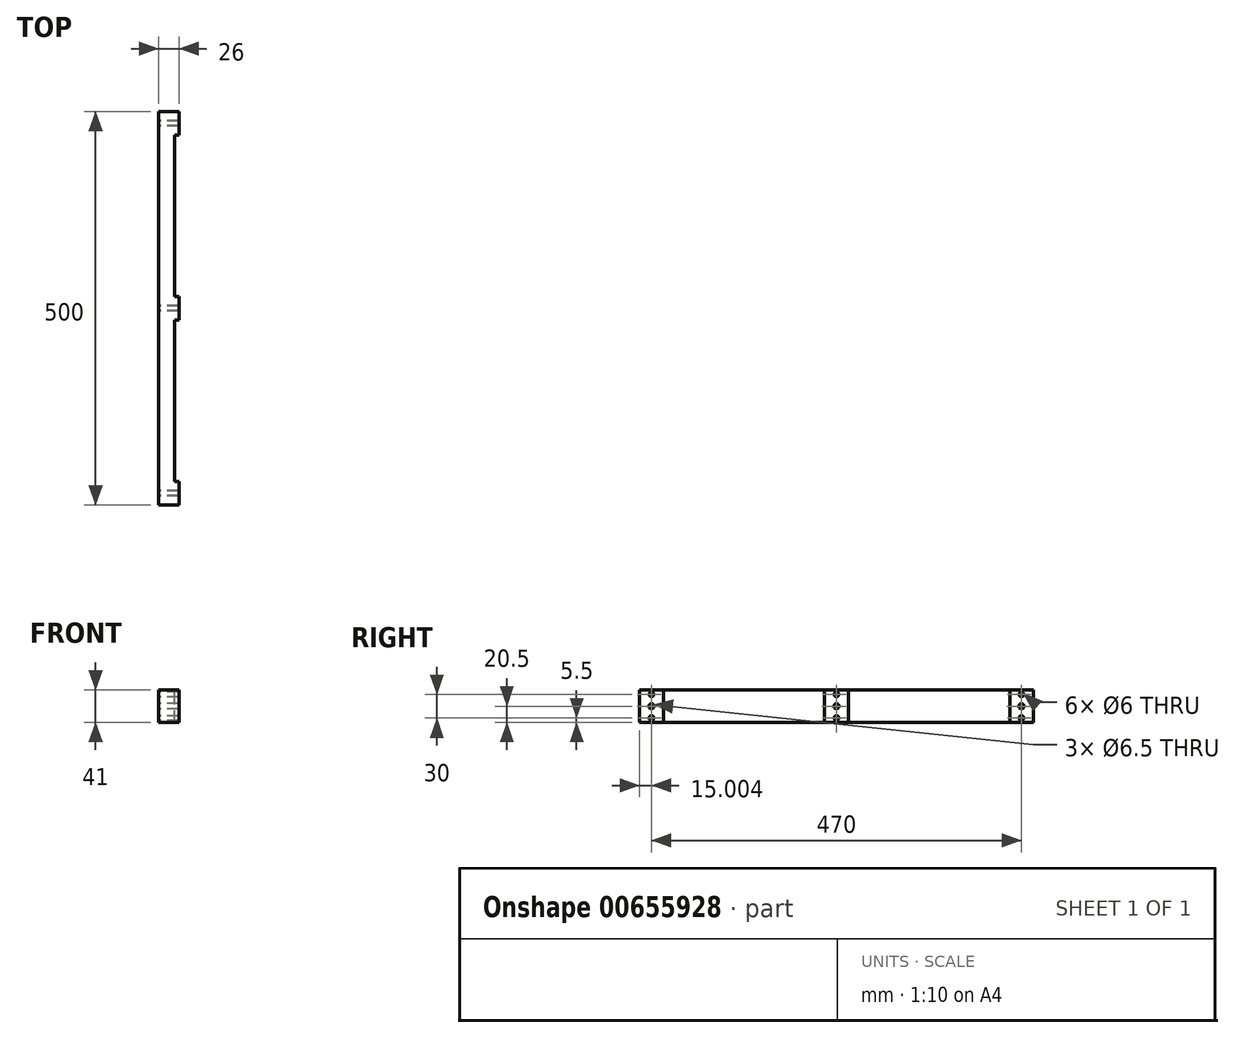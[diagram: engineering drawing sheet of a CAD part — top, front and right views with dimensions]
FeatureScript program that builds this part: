
annotation { "Feature Type Name" : "Feature", "Feature Type Description" : "" }
export const myFeature = defineFeature(function(context is Context, id is Id, definition is map)
    precondition{}
    {
        {
            var Q0;
            Q0=qCreatedBy(makeId("Right.planeOp"),FACE);
            var sketch = newSketch(context, id + "F0", { "sketchPlane" : qUnion([Q0])});
            skLineSegment(sketch, "E0.bottom", {"start": v(-358.97, 48.34) * mm, "end": v(141.03, 48.34) * mm});
            skLineSegment(sketch, "E0.top", {"start": v(-358.97, 7.34) * mm, "end": v(141.03, 7.34) * mm});
            skLineSegment(sketch, "E0.left", {"start": v(-358.97, 48.34) * mm, "end": v(-358.97, 7.34) * mm});
            skLineSegment(sketch, "E0.right", {"start": v(141.03, 48.34) * mm, "end": v(141.03, 7.34) * mm});
            skCircle(sketch, "E1", {"center": v(-343.97, 27.84) * mm, "radius": 3.25 * mm});
            skCircle(sketch, "E2", {"center": v(-108.97, 27.84) * mm, "radius": 3.25 * mm});
            skCircle(sketch, "E3", {"center": v(126.03, 27.84) * mm, "radius": 3.25 * mm});
            skCircle(sketch, "E4", {"center": v(-343.97, 42.84) * mm, "radius": 3 * mm});
            skCircle(sketch, "E5", {"center": v(-343.97, 12.84) * mm, "radius": 3 * mm});
            skCircle(sketch, "E6", {"center": v(-343.97, 27.84) * mm, "radius": 10 * mm, "construction": true});
            skCircle(sketch, "E7", {"center": v(-108.97, 42.84) * mm, "radius": 3 * mm});
            skCircle(sketch, "E8", {"center": v(-108.97, 12.84) * mm, "radius": 3 * mm});
            skCircle(sketch, "E9", {"center": v(126.03, 42.84) * mm, "radius": 3 * mm});
            skCircle(sketch, "E10", {"center": v(126.03, 12.84) * mm, "radius": 3 * mm});
            skCircle(sketch, "E11", {"center": v(-108.97, 27.84) * mm, "radius": 10 * mm, "construction": true});
            skCircle(sketch, "E12", {"center": v(126.03, 27.84) * mm, "radius": 10 * mm, "construction": true});
            skSolve(sketch);
        }
        {
            var Q0;
            Q0=makeQuery(id+"F0.imprint","IMPRINT",FACE,{"disambiguationData":[TD([[makeQuery(id+"F0.imprint","IMPRINT",EDGE,{"derivedFrom":sQuery(id+"F0.wireOp",EDGE,"E0.bottom")}),-1.0]])]});
            extrude(context, id + "F1", {"entities" : qUnion([Q0]), "depth" : 26 * mm, "offsetDistance" : 25 * mm});
        }
        {
            var Q0;
            Q0=makeQuery(id+"F1.opExtrude","SWEPT_FACE",FACE,{"disambiguationData":[OSD([sQuery(id+"F0.wireOp",EDGE,"E0.bottom")])]});
            var sketch = newSketch(context, id + "F2", { "sketchPlane" : qUnion([Q0])});
            skLineSegment(sketch, "E13.bottom", {"start": v(26, -328.97) * mm, "end": v(20, -328.97) * mm});
            skLineSegment(sketch, "E13.top", {"start": v(26, -123.97) * mm, "end": v(20, -123.97) * mm});
            skLineSegment(sketch, "E13.left", {"start": v(26, -328.97) * mm, "end": v(26, -123.97) * mm});
            skLineSegment(sketch, "E13.right", {"start": v(20, -328.97) * mm, "end": v(20, -123.97) * mm});
            skLineSegment(sketch, "E14.bottom", {"start": v(26, 111.03) * mm, "end": v(20, 111.03) * mm});
            skLineSegment(sketch, "E14.top", {"start": v(26, -93.97) * mm, "end": v(20, -93.97) * mm});
            skLineSegment(sketch, "E14.left", {"start": v(26, 111.03) * mm, "end": v(26, -93.97) * mm});
            skLineSegment(sketch, "E14.right", {"start": v(20, 111.03) * mm, "end": v(20, -93.97) * mm});
            skSolve(sketch);
        }
        {
            var Q0;
            Q0 = qSketchRegion(id + "F2", true);
            var Q1;
            Q1=makeQuery(id+"F1.opExtrude","SWEPT_FACE",FACE,{"disambiguationData":[OSD([sQuery(id+"F0.wireOp",EDGE,"E0.top")])]});
            extrude(context, id + "F3", {"entities" : qUnion([Q0]), "operationType" : NewBodyOperationType.REMOVE, "endBound" : BoundingType.UP_TO_SURFACE, "oppositeDirection" : true, "depth" : 25 * mm, "endBoundEntityFace" : qUnion([Q1]), "offsetDistance" : 25 * mm});
        }
    });
